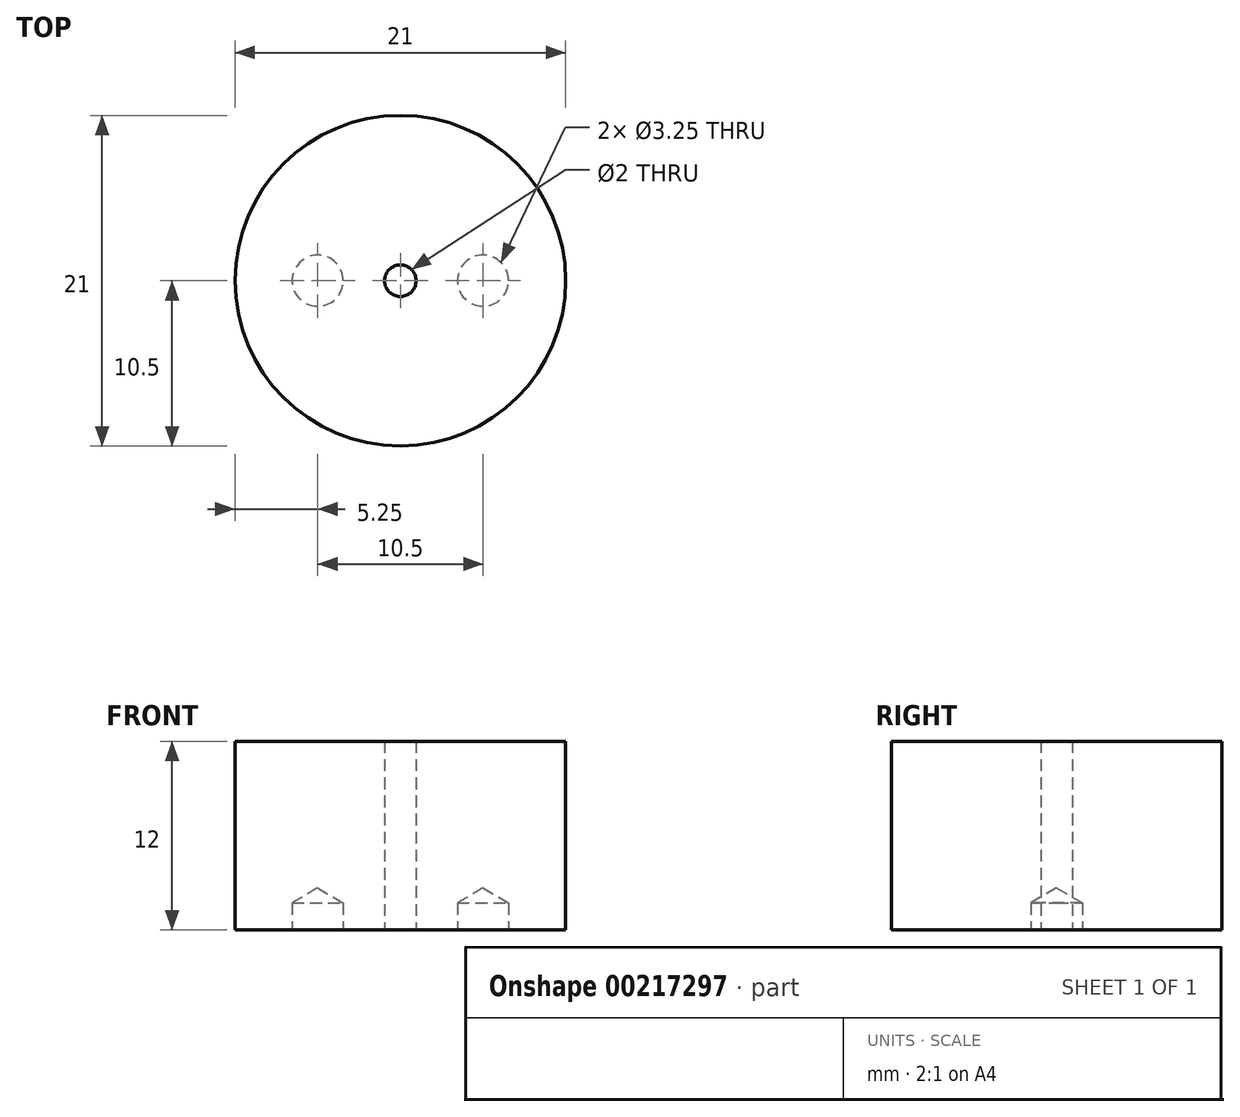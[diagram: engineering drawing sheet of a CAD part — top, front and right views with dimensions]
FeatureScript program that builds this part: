
annotation { "Feature Type Name" : "Feature", "Feature Type Description" : "" }
export const myFeature = defineFeature(function(context is Context, id is Id, definition is map)
    precondition{}
    {
        {
            var Q0;
            Q0=qCreatedBy(makeId("Top.planeOp"),FACE);
            var sketch = newSketch(context, id + "F0", { "sketchPlane" : qUnion([Q0])});
            skCircle(sketch, "E0", {"center": v(0, 0) * mm, "radius": 10.5 * mm});
            skCircle(sketch, "E1", {"center": v(0, 0) * mm, "radius": 1 * mm});
            skLineSegment(sketch, "E2", {"start": v(0, 0) * mm, "end": v(-5.25, 0) * mm});
            skLineSegment(sketch, "E3", {"start": v(-5.25, 0) * mm, "end": v(5.25, 0) * mm});
            skCircle(sketch, "E4", {"center": v(-5.25, 0) * mm, "radius": 1.63 * mm});
            skCircle(sketch, "E5", {"center": v(5.25, 0) * mm, "radius": 1.63 * mm});
            skSolve(sketch);
        }
        {
            var Q0;
            Q0=makeQuery(id+"F0.imprint","IMPRINT",FACE,{"disambiguationData":[TD([[makeQuery(id+"F0.imprint","IMPRINT",EDGE,{"derivedFrom":sQuery(id+"F0.wireOp",EDGE,"E0")}),1.0]])]});
            var Q1;
            Q1=makeQuery(id+"F0.imprint","IMPRINT",FACE,{"disambiguationData":[TD([[makeQuery(id+"F0.imprint","IMPRINT",EDGE,{"derivedFrom":sQuery(id+"F0.wireOp",EDGE,"E4")}),1.0]])]});
            var Q2;
            Q2=makeQuery(id+"F0.imprint","IMPRINT",FACE,{"disambiguationData":[TD([[makeQuery(id+"F0.imprint","IMPRINT",EDGE,{"derivedFrom":sQuery(id+"F0.wireOp",EDGE,"E5")}),1.0]])]});
            extrude(context, id + "F1", {"entities" : qUnion([Q0, Q1, Q2]), "depth" : 12 * mm});
        }
        {
            var Q0;
            Q0=sQuery(id+"F0.wireOp",VERTEX,"E4.center");
            var Q1;
            Q1=sQuery(id+"F0.wireOp",VERTEX,"E5.center");
            var Q2;
            Q2=makeQuery(id+"F1.opExtrude","SWEPT_BODY",BODY,{"disambiguationData":[OSD([sQuery(id+"F0.wireOp",EDGE,"E0"),sQuery(id+"F0.wireOp",EDGE,"E1")])]});
            hole(context, id + "F2", {"style" : HoleStyle.SIMPLE, "endStyle" : HoleEndStyle.BLIND, "oppositeDirection" : true, "holeDiameter" : 3.25 * mm, "holeDepth" : 1.72 * mm, "locations" : qUnion([Q0, Q1]), "scope" : qUnion([Q2])});
        }
    });
